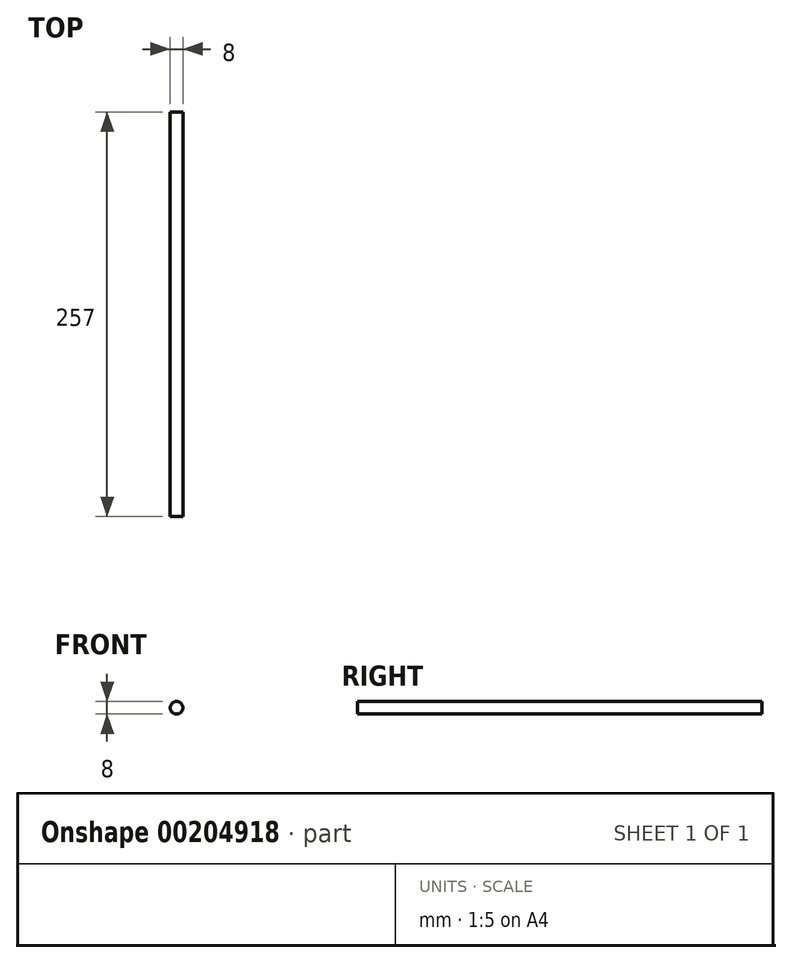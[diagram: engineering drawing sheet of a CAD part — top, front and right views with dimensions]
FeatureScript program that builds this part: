
annotation { "Feature Type Name" : "Feature", "Feature Type Description" : "" }
export const myFeature = defineFeature(function(context is Context, id is Id, definition is map)
    precondition{}
    {
        {
            var Q0;
            Q0=qCreatedBy(makeId("Front.planeOp"),FACE);
            var sketch = newSketch(context, id + "F0", { "sketchPlane" : qUnion([Q0])});
            skCircle(sketch, "E0", {"center": v(0, 0) * mm, "radius": 4 * mm});
            skSolve(sketch);
        }
        {
            var Q0;
            Q0=makeQuery(id+"F0.imprint","IMPRINT",FACE,{"disambiguationData":[TD([[makeQuery(id+"F0.imprint","IMPRINT",EDGE,{"derivedFrom":sQuery(id+"F0.wireOp",EDGE,"E0")}),1.0]])]});
            extrude(context, id + "F1", {"entities" : qUnion([Q0]), "depth" : 300 * mm});
        }
        {
            var Q0;
            Q0=makeQuery(id+"F1.opExtrude","CAP_FACE",FACE,{"disambiguationData":[OSD([sQuery(id+"F0.wireOp",EDGE,"E0")])],"isStart":false});
            extrude(context, id + "F2", {"entities" : qUnion([Q0]), "operationType" : NewBodyOperationType.REMOVE, "oppositeDirection" : true, "depth" : (300 - 257) * mm});
        }
    });
